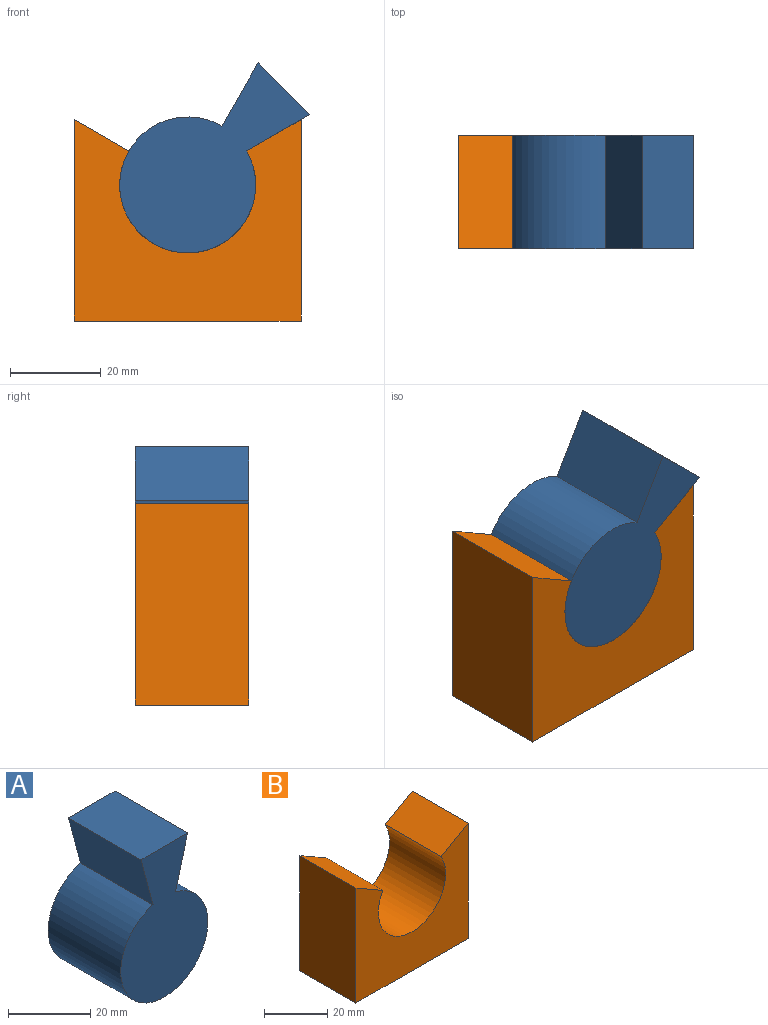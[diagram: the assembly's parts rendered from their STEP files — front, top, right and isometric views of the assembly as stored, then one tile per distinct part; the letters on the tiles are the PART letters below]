
ASSEMBLY  parts=2 mates=1
PART A: 6 faces, bbox 30x25x45 mm
  f0: cylinder r=15mm len=30mm, axis (0,1,0), area 2159.8mm2, adj f1,f3,f4,f5
  f1: plane 25x15.51mm, normal (0.97,0,-0.26), area 401.5mm2, adj f0,f2,f4,f5
  f2: plane 25x16.08mm, normal (0,0,1), area 401.9mm2, adj f1,f3,f4,f5
  f3: plane 25x15.51mm, normal (-0.97,0,-0.26), area 401.5mm2, adj f0,f2,f4,f5
  f4: plane 45x30mm, normal (0,-1,0), area 889.1mm2, adj f0,f1,f2,f3
  f5: plane 45x30mm, normal (0,1,0), area 889.1mm2, adj f0,f1,f2,f3
PART B: 8 faces, bbox 50x25x44.4 mm
  f0: plane 44.43x25mm, normal (1,0,0), area 1110.8mm2, adj f1,f5,f6,f7
  f1: plane 25x12.01mm, normal (-0.5,0,0.87), area 346.7mm2, adj f0,f2,f6,f7
  f2: cylinder r=15mm len=30mm, axis (0,1,0), area 1570.8mm2, adj f1,f3,f6,f7
  f3: plane 25x12.01mm, normal (0.5,0,0.87), area 346.7mm2, adj f2,f4,f6,f7
  f4: plane 44.43x25mm, normal (-1,0,0), area 1110.8mm2, adj f3,f5,f6,f7
  f5: plane 50x25mm, normal (0,0,-1), area 1250mm2, adj f0,f4,f6,f7
  f6: plane 50x44.43mm, normal (0,-1,0), area 1389.6mm2, adj f0,f1,f2,f3,f4,f5
  f7: plane 50x44.43mm, normal (0,1,0), area 1389.6mm2, adj f0,f1,f2,f3,f4,f5
PLACE A rot(axis=(0,1,0),45deg) t=(-11.28,11.42,8.14)mm
PLACE B t=(-11.28,11.42,8.14)mm fixed
MATE revolute A.f0 <-> B.f2  axis (0,-1,0) through (-11.28,-13.58,8.14)mm
